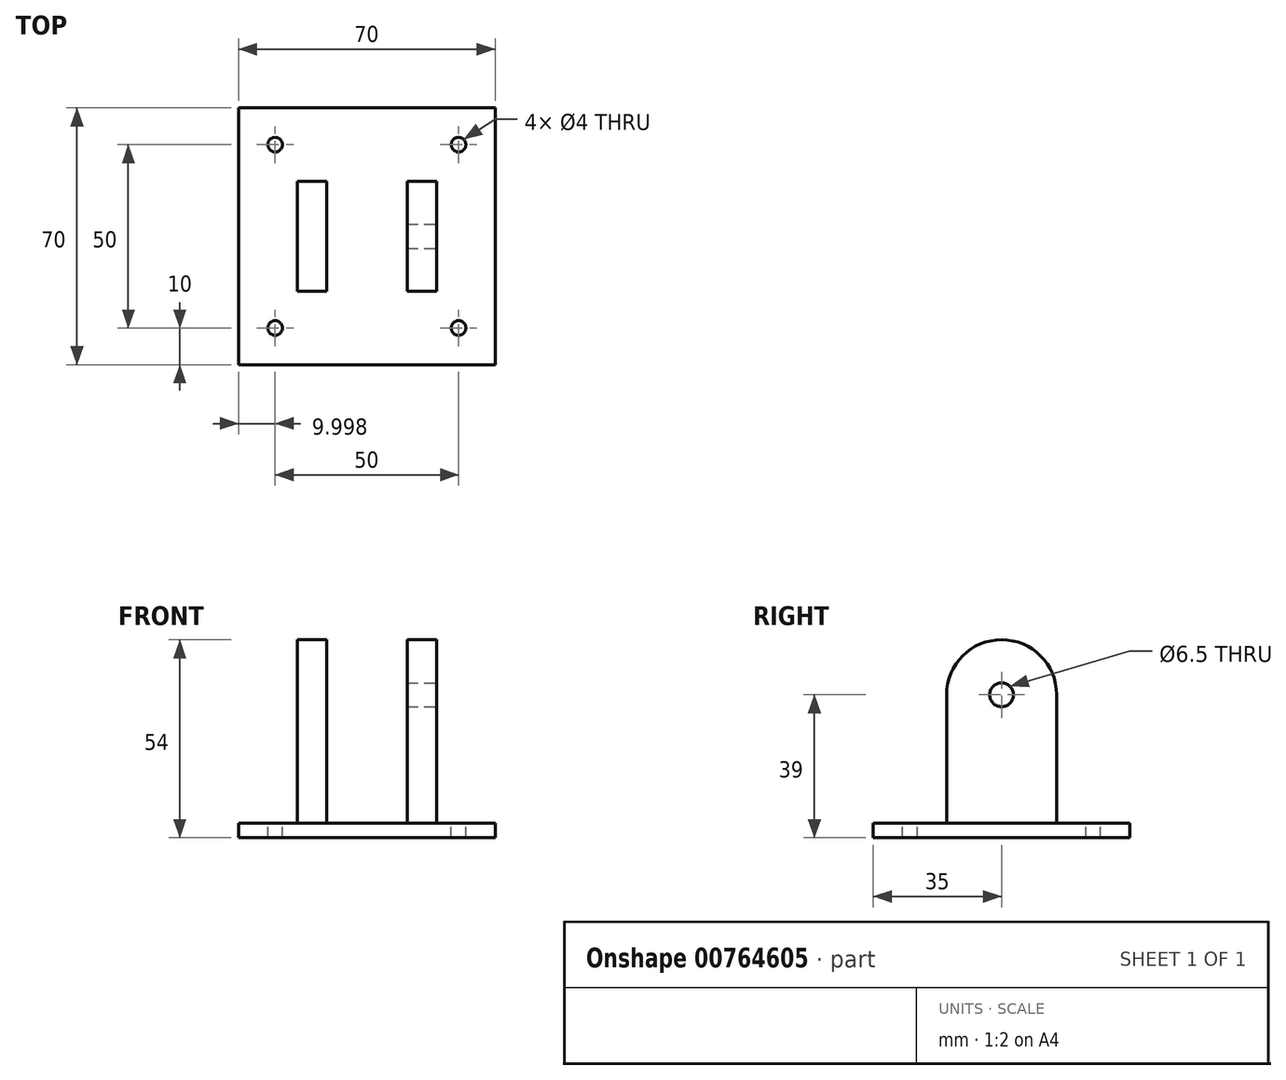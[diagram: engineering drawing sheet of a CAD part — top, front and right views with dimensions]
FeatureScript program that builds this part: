
annotation { "Feature Type Name" : "Feature", "Feature Type Description" : "" }
export const myFeature = defineFeature(function(context is Context, id is Id, definition is map)
    precondition{}
    {
        {
            var Q0;
            Q0=qCreatedBy(makeId("Top.planeOp"),FACE);
            var sketch = newSketch(context, id + "F0", { "sketchPlane" : qUnion([Q0])});
            skLineSegment(sketch, "E0.bottom", {"start": v(-33.96, 70) * mm, "end": v(36.04, 70) * mm});
            skLineSegment(sketch, "E0.top", {"start": v(-33.96, 0) * mm, "end": v(36.04, 0) * mm});
            skLineSegment(sketch, "E0.left", {"start": v(-33.96, 70) * mm, "end": v(-33.96, 0) * mm});
            skLineSegment(sketch, "E0.right", {"start": v(36.04, 70) * mm, "end": v(36.04, 0) * mm});
            skSolve(sketch);
        }
        {
            var Q0;
            Q0 = qSketchRegion(id + "F0", true);
            extrude(context, id + "F1", {"entities" : qUnion([Q0]), "depth" : 4 * mm, "offsetDistance" : 25.4 * mm});
        }
        {
            var Q0;
            Q0=makeQuery(id+"F1.opExtrude","CAP_FACE",FACE,{"disambiguationData":[OSD([sQuery(id+"F0.wireOp",EDGE,"E0.bottom"),sQuery(id+"F0.wireOp",EDGE,"E0.top"),sQuery(id+"F0.wireOp",EDGE,"E0.left"),sQuery(id+"F0.wireOp",EDGE,"E0.right")])],"isStart":false});
            var sketch = newSketch(context, id + "F2", { "sketchPlane" : qUnion([Q0])});
            skLineSegment(sketch, "E1.bottom", {"start": v(-17.96, 50) * mm, "end": v(-9.96, 50) * mm});
            skLineSegment(sketch, "E1.top", {"start": v(-17.96, 20) * mm, "end": v(-9.96, 20) * mm});
            skLineSegment(sketch, "E1.left", {"start": v(-17.96, 50) * mm, "end": v(-17.96, 20) * mm});
            skLineSegment(sketch, "E1.right", {"start": v(-9.96, 50) * mm, "end": v(-9.96, 20) * mm});
            skLineSegment(sketch, "E2.bottom", {"start": v(12.04, 50) * mm, "end": v(20.04, 50) * mm});
            skLineSegment(sketch, "E2.top", {"start": v(12.04, 20) * mm, "end": v(20.04, 20) * mm});
            skLineSegment(sketch, "E2.left", {"start": v(12.04, 50) * mm, "end": v(12.04, 20) * mm});
            skLineSegment(sketch, "E2.right", {"start": v(20.04, 50) * mm, "end": v(20.04, 20) * mm});
            skSolve(sketch);
        }
        {
            var Q0;
            Q0=makeQuery(id+"F2.imprint","IMPRINT",FACE,{"disambiguationData":[TD([[makeQuery(id+"F2.imprint","IMPRINT",EDGE,{"derivedFrom":sQuery(id+"F2.wireOp",EDGE,"E1.bottom")}),-1.0]])]});
            var Q1;
            Q1=makeQuery(id+"F2.imprint","IMPRINT",FACE,{"disambiguationData":[TD([[makeQuery(id+"F2.imprint","IMPRINT",EDGE,{"derivedFrom":sQuery(id+"F2.wireOp",EDGE,"E2.bottom")}),-1.0]])]});
            extrude(context, id + "F3", {"entities" : qUnion([Q0, Q1]), "operationType" : NewBodyOperationType.ADD, "depth" : 50 * mm, "offsetDistance" : 25 * mm});
        }
        {
            var Q0;
            Q0=makeQuery(id+"F3.opExtrude","CAP_EDGE",EDGE,{"disambiguationData":[OSD([sQuery(id+"F2.wireOp",EDGE,"E1.top")])],"isStart":false});
            var Q1;
            Q1=makeQuery(id+"F3.opExtrude","CAP_EDGE",EDGE,{"disambiguationData":[OSD([sQuery(id+"F2.wireOp",EDGE,"E1.bottom")])],"isStart":false});
            var Q2;
            Q2=makeQuery(id+"F3.opExtrude","CAP_EDGE",EDGE,{"disambiguationData":[OSD([sQuery(id+"F2.wireOp",EDGE,"E2.top")])],"isStart":false});
            var Q3;
            Q3=makeQuery(id+"F3.opExtrude","CAP_EDGE",EDGE,{"disambiguationData":[OSD([sQuery(id+"F2.wireOp",EDGE,"E2.bottom")])],"isStart":false});
            fillet(context, id + "F4", {"entities" : qUnion([Q0, Q1, Q2, Q3]), "radius" : 15 * mm, "tangentPropagation" : true, "allowEdgeOverflow" : false});
        }
        {
            var Q0;
            Q0=makeQuery(id+"F1.opExtrude","CAP_FACE",FACE,{"disambiguationData":[OSD([sQuery(id+"F0.wireOp",EDGE,"E0.bottom"),sQuery(id+"F0.wireOp",EDGE,"E0.top"),sQuery(id+"F0.wireOp",EDGE,"E0.left"),sQuery(id+"F0.wireOp",EDGE,"E0.right")])],"isStart":false});
            var sketch = newSketch(context, id + "F5", { "sketchPlane" : qUnion([Q0])});
            skPoint(sketch, "E3", {"position": v(-23.96, 60) * mm});
            skPoint(sketch, "E4", {"position": v(26.04, 60) * mm});
            skPoint(sketch, "E5", {"position": v(26.04, 10) * mm});
            skPoint(sketch, "E6", {"position": v(-23.96, 10) * mm});
            skSolve(sketch);
        }
        {
            var Q0;
            Q0=makeQuery(id+"F3.opExtrude","SWEPT_FACE",FACE,{"disambiguationData":[OSD([sQuery(id+"F2.wireOp",EDGE,"E2.right")])]});
            var sketch = newSketch(context, id + "F6", { "sketchPlane" : qUnion([Q0])});
            skPoint(sketch, "E7", {"position": v(35, 39) * mm});
            skSolve(sketch);
        }
        {
            var Q0;
            Q0=sQuery(id+"F6.wireOp",VERTEX,"E7");
            var Q1;
            Q1=makeQuery(id+"F1.opExtrude","SWEPT_BODY",BODY,{"disambiguationData":[OSD([sQuery(id+"F0.wireOp",EDGE,"E0.bottom"),sQuery(id+"F0.wireOp",EDGE,"E0.top"),sQuery(id+"F0.wireOp",EDGE,"E0.left"),sQuery(id+"F0.wireOp",EDGE,"E0.right")])]});
            hole(context, id + "F7", {"style" : HoleStyle.SIMPLE, "endStyle" : HoleEndStyle.BLIND, "holeDiameter" : 6.5 * mm, "majorDiameter" : 5 * mm, "holeDepth" : 15 * mm, "isTappedThrough" : true, "tappedDepth" : 12 * mm, "tapClearance" : 3, "locations" : qUnion([Q0]), "scope" : qUnion([Q1])});
        }
        {
            var Q0;
            Q0=sQuery(id+"F5.wireOp",VERTEX,"E6");
            var Q1;
            Q1=sQuery(id+"F5.wireOp",VERTEX,"E5");
            var Q2;
            Q2=sQuery(id+"F5.wireOp",VERTEX,"E4");
            var Q3;
            Q3=sQuery(id+"F5.wireOp",VERTEX,"E3");
            var Q4;
            Q4=makeQuery(id+"F1.opExtrude","SWEPT_BODY",BODY,{"disambiguationData":[OSD([sQuery(id+"F0.wireOp",EDGE,"E0.bottom"),sQuery(id+"F0.wireOp",EDGE,"E0.top"),sQuery(id+"F0.wireOp",EDGE,"E0.left"),sQuery(id+"F0.wireOp",EDGE,"E0.right")])]});
            hole(context, id + "F8", {"style" : HoleStyle.SIMPLE, "endStyle" : HoleEndStyle.BLIND, "holeDiameter" : 4 * mm, "majorDiameter" : 5 * mm, "holeDepth" : 15 * mm, "isTappedThrough" : true, "tappedDepth" : 12 * mm, "tapClearance" : 3, "locations" : qUnion([Q0, Q1, Q2, Q3]), "scope" : qUnion([Q4])});
        }
    });
